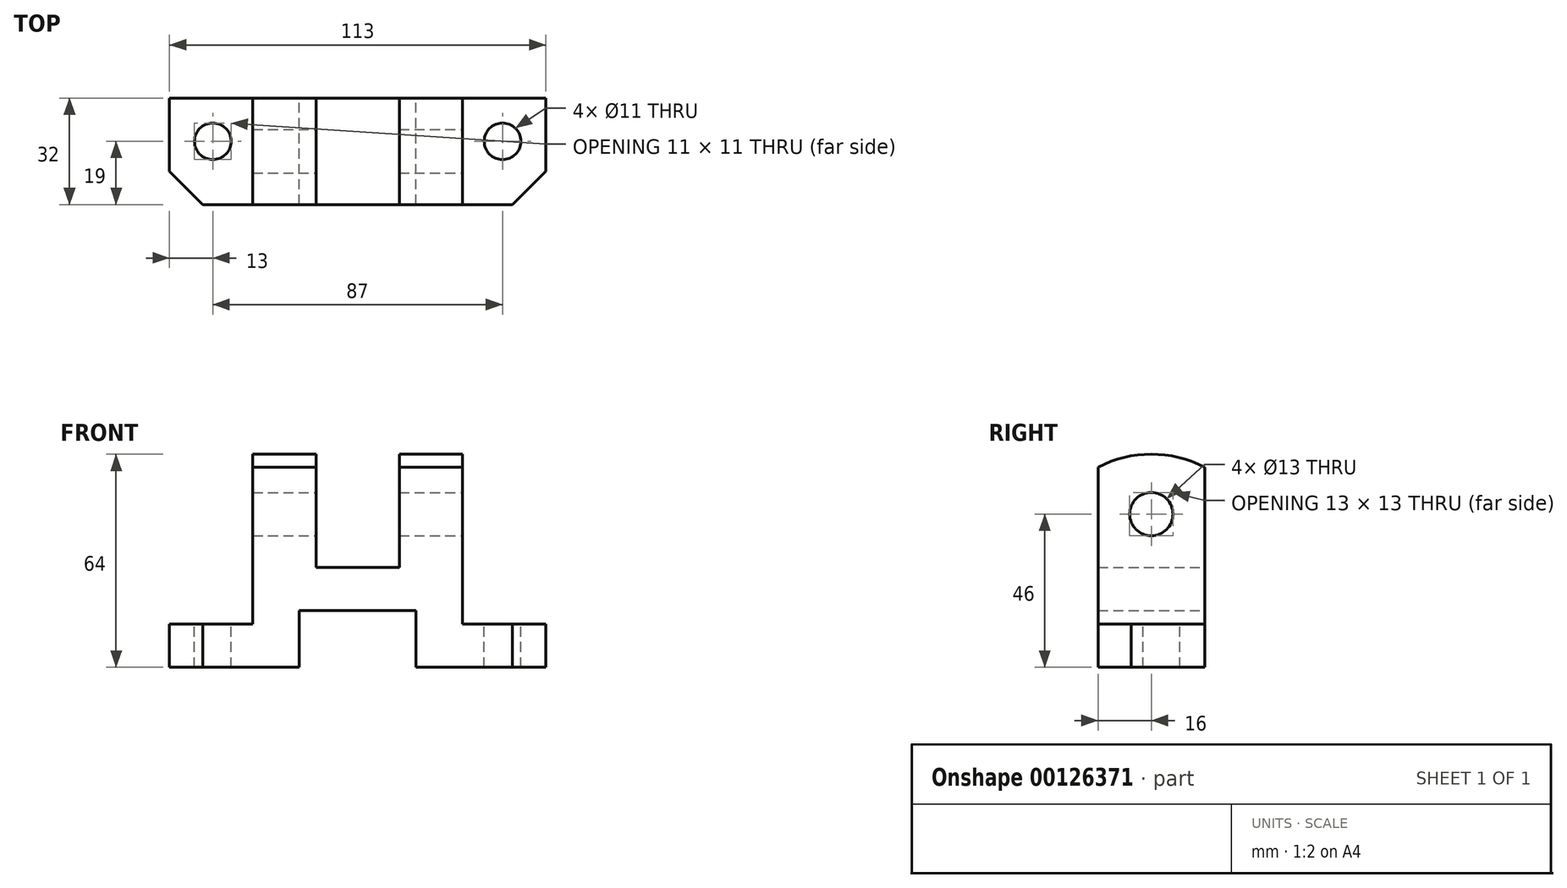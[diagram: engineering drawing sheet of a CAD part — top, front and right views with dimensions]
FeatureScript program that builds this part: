
annotation { "Feature Type Name" : "Feature", "Feature Type Description" : "" }
export const myFeature = defineFeature(function(context is Context, id is Id, definition is map)
    precondition{}
    {
        {
            var Q0;
            Q0=qCreatedBy(makeId("Front.planeOp"),FACE);
            var sketch = newSketch(context, id + "F0", { "sketchPlane" : qUnion([Q0])});
            skLineSegment(sketch, "E0", {"start": v(0, 0) * mm, "end": v(0, 89.61) * mm, "construction": true});
            skLineSegment(sketch, "E1", {"start": v(0, 17) * mm, "end": v(-17.5, 17) * mm});
            skLineSegment(sketch, "E2", {"start": v(-17.5, 17) * mm, "end": v(-17.5, 0) * mm});
            skLineSegment(sketch, "E3", {"start": v(-17.5, 0) * mm, "end": v(-56.5, 0) * mm});
            skLineSegment(sketch, "E4", {"start": v(-56.5, 0) * mm, "end": v(-56.5, 13) * mm});
            skLineSegment(sketch, "E5", {"start": v(-56.5, 13) * mm, "end": v(-31.5, 13) * mm});
            skLineSegment(sketch, "E6", {"start": v(-31.5, 13) * mm, "end": v(-31.5, 64) * mm});
            skLineSegment(sketch, "E7", {"start": v(-31.5, 64) * mm, "end": v(-12.5, 64) * mm});
            skLineSegment(sketch, "E8", {"start": v(-12.5, 64) * mm, "end": v(-12.5, 30) * mm});
            skLineSegment(sketch, "E9", {"start": v(-12.5, 30) * mm, "end": v(0, 30) * mm});
            skLineSegment(sketch, "E10.MirrorCS", {"start": v(0, 17) * mm, "end": v(17.5, 17) * mm});
            skLineSegment(sketch, "E11.MirrorCS", {"start": v(12.5, 30) * mm, "end": v(0, 30) * mm});
            skLineSegment(sketch, "E12.MirrorCS", {"start": v(12.5, 64) * mm, "end": v(12.5, 30) * mm});
            skLineSegment(sketch, "E13.MirrorCS", {"start": v(31.5, 64) * mm, "end": v(12.5, 64) * mm});
            skLineSegment(sketch, "E14.MirrorCS", {"start": v(31.5, 13) * mm, "end": v(31.5, 64) * mm});
            skLineSegment(sketch, "E15.MirrorCS", {"start": v(56.5, 13) * mm, "end": v(31.5, 13) * mm});
            skLineSegment(sketch, "E16.MirrorCS", {"start": v(56.5, 0) * mm, "end": v(56.5, 13) * mm});
            skLineSegment(sketch, "E17.MirrorCS", {"start": v(17.5, 0) * mm, "end": v(56.5, 0) * mm});
            skLineSegment(sketch, "E18.MirrorCS", {"start": v(17.5, 17) * mm, "end": v(17.5, 0) * mm});
            skSolve(sketch);
        }
        {
            var Q0;
            Q0 = qSketchRegion(id + "F0", true);
            extrude(context, id + "F1", {"entities" : qUnion([Q0]), "depth" : 32 * mm});
        }
        {
            var Q0;
            Q0=makeQuery(id+"F1.opExtrude","SWEPT_FACE",FACE,{"disambiguationData":[OSD([sQuery(id+"F0.wireOp",EDGE,"E15.MirrorCS")])]});
            var sketch = newSketch(context, id + "F2", { "sketchPlane" : qUnion([Q0])});
            skCircle(sketch, "E19", {"center": v(-43.5, -13) * mm, "radius": 5.5 * mm});
            skLineSegment(sketch, "E20", {"start": v(0, 0) * mm, "end": v(0, -52.4) * mm, "construction": true});
            skLineSegment(sketch, "E21", {"start": v(-56.5, -22) * mm, "end": v(-46.5, -32) * mm});
            skLineSegment(sketch, "E22", {"start": v(-46.5, -32) * mm, "end": v(-56.5, -32) * mm});
            skLineSegment(sketch, "E23", {"start": v(-56.5, -32) * mm, "end": v(-56.5, -22) * mm});
            skLineSegment(sketch, "E24.MirrorCS", {"start": v(46.5, -32) * mm, "end": v(56.5, -32) * mm});
            skLineSegment(sketch, "E25.MirrorCS", {"start": v(56.5, -22) * mm, "end": v(46.5, -32) * mm});
            skLineSegment(sketch, "E26.MirrorCS", {"start": v(56.5, -32) * mm, "end": v(56.5, -22) * mm});
            skCircle(sketch, "E27.MirrorC", {"center": v(43.5, -13) * mm, "radius": 5.5 * mm});
            skSolve(sketch);
        }
        {
            var Q0;
            Q0 = qSketchRegion(id + "F2", true);
            extrude(context, id + "F3", {"entities" : qUnion([Q0]), "operationType" : NewBodyOperationType.REMOVE, "endBound" : BoundingType.THROUGH_ALL, "oppositeDirection" : true, "depth" : 25 * mm});
        }
        {
            var Q0;
            Q0=makeQuery(id+"F1.opExtrude","SWEPT_FACE",FACE,{"disambiguationData":[OSD([sQuery(id+"F0.wireOp",EDGE,"E14.MirrorCS")])]});
            var sketch = newSketch(context, id + "F4", { "sketchPlane" : qUnion([Q0])});
            skCircle(sketch, "E28", {"center": v(-16, 46) * mm, "radius": 6.5 * mm});
            skSolve(sketch);
        }
        {
            var Q0;
            Q0 = qSketchRegion(id + "F4", true);
            extrude(context, id + "F5", {"entities" : qUnion([Q0]), "operationType" : NewBodyOperationType.REMOVE, "endBound" : BoundingType.THROUGH_ALL, "oppositeDirection" : true, "depth" : 25 * mm});
        }
        {
            var Q0;
            Q0=makeQuery(id+"F1.opExtrude","SWEPT_FACE",FACE,{"disambiguationData":[OSD([sQuery(id+"F0.wireOp",EDGE,"E14.MirrorCS")])]});
            var sketch = newSketch(context, id + "F6", { "sketchPlane" : qUnion([Q0])});
            skArc(sketch, "E29", {"start": v(0, 60.13) * mm, "mid": v(-16, 64) * mm, "end": v(-32, 60.13) * mm});
            skLineSegment(sketch, "E30.0", {"start": v(-32, 13) * mm, "end": v(-32, 64) * mm});
            skLineSegment(sketch, "E30.1", {"start": v(-32, 64) * mm, "end": v(0, 64) * mm});
            skLineSegment(sketch, "E30.2", {"start": v(0, 13) * mm, "end": v(0, 64) * mm});
            skSolve(sketch);
        }
        {
            var Q0;
            Q0 = qSketchRegion(id + "F6", true);
            extrude(context, id + "F7", {"entities" : qUnion([Q0]), "operationType" : NewBodyOperationType.REMOVE, "endBound" : BoundingType.THROUGH_ALL, "oppositeDirection" : true, "depth" : 25 * mm});
        }
    });
